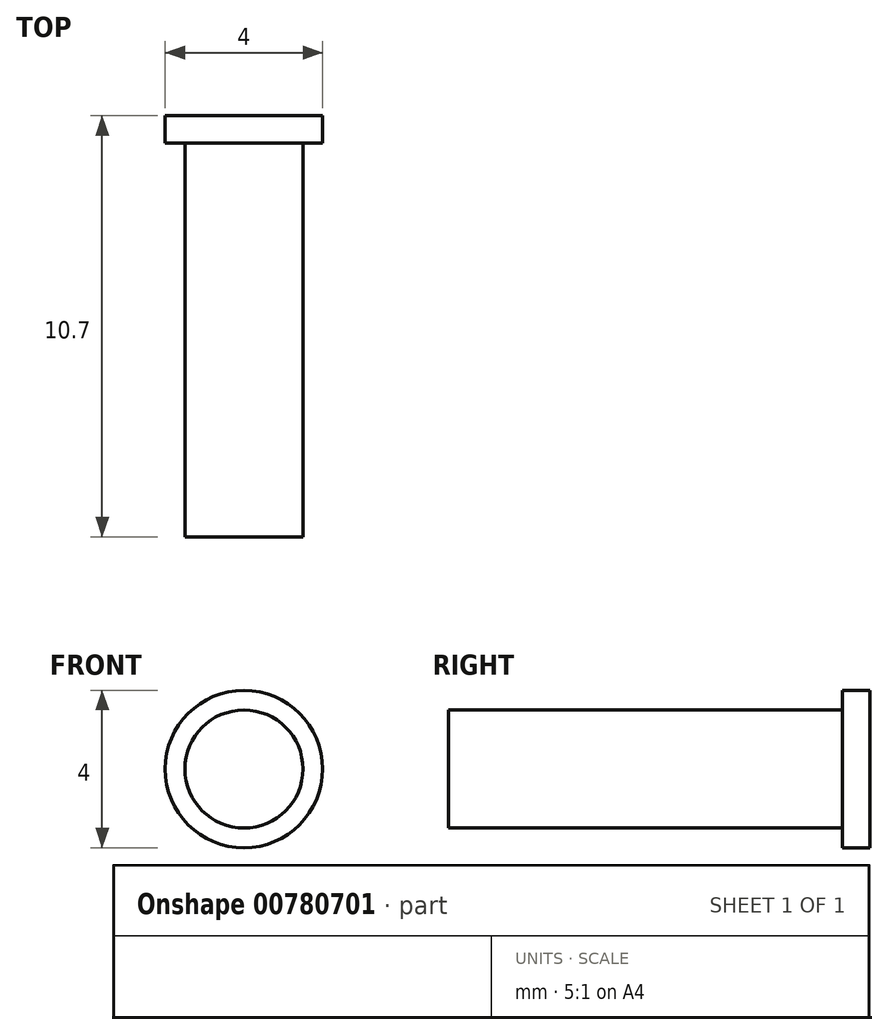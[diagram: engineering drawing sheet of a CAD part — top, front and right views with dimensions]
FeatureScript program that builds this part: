
annotation { "Feature Type Name" : "Feature", "Feature Type Description" : "" }
export const myFeature = defineFeature(function(context is Context, id is Id, definition is map)
    precondition{}
    {
        {
            var Q0;
            Q0=qCreatedBy(makeId("Front.planeOp"),FACE);
            var sketch = newSketch(context, id + "F0", { "sketchPlane" : qUnion([Q0])});
            skCircle(sketch, "E0", {"center": v(0, 0) * mm, "radius": 2 * mm});
            skSolve(sketch);
        }
        {
            var Q0;
            Q0=makeQuery(id+"F0.imprint","IMPRINT",FACE,{"disambiguationData":[TD([[makeQuery(id+"F0.imprint","IMPRINT",EDGE,{"derivedFrom":sQuery(id+"F0.wireOp",EDGE,"E0")}),1.0]])]});
            extrude(context, id + "F1", {"entities" : qUnion([Q0]), "depth" : .7 * mm, "offsetDistance" : 25 * mm});
        }
        {
            var Q0;
            Q0=makeQuery(id+"F1.opExtrude","CAP_FACE",FACE,{"disambiguationData":[OSD([sQuery(id+"F0.wireOp",EDGE,"E0")])],"isStart":false});
            var sketch = newSketch(context, id + "F2", { "sketchPlane" : qUnion([Q0])});
            skCircle(sketch, "E1", {"center": v(0, 0) * mm, "radius": 1.5 * mm});
            skSolve(sketch);
        }
        {
            var Q0;
            Q0 = qSketchRegion(id + "F2", true);
            extrude(context, id + "F3", {"entities" : qUnion([Q0]), "operationType" : NewBodyOperationType.ADD, "depth" : 10 * mm, "offsetDistance" : 25 * mm});
        }
    });
